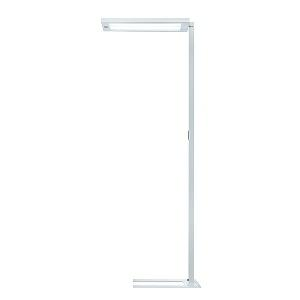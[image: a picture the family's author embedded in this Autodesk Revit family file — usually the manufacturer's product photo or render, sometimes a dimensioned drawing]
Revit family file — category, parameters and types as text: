
# Revit family: lavigo_-_dps_9000_840_d_g2_00807247_5373
name_source: partatom
category: Lighting Fixtures
units: mm (PartAtom-declared; Revit-internal decimal feet)

## family parameters
Cut with Voids When Loaded = No
Host = Face
Light Source = No
Part Type = Normal
Room Calculation Point = No
Round Connector Dimension = Use Diameter
Shared = No

## types (1)
- LAVIGO - DPS 9000/840/D/G2 (1 x LED, 8950 lm, 4000K)
    Apparent Load = 63 VA
    CIE Flux Codes = 60 87 97 20 100
    Color Rendering = 80-89
    Color Temperature = 4000K
    Control Gear = Electronic ballast
    Default Elevation = 1800 mm
    Description = DPS 9000/840/D/G2|Free-standing luminaire|light source: LED|work equipment: Electronic ballast|connected load: 220-240 V, 50/60 Hz|Power consumption: approx. 63 W|standby: approx. 0,50|power factor: approx. 0,910|luminous flux: 8950 lm|luminous efficacy: 142 lm/W|light distribution: Direct/indirect|direct ratio: approx. 20 %|colour temperature: Cold white, ca. 4000 K|color rendering index (CRI): >= 80|chromaticity tolerance:  3 SDCM|technology: Continuously dimmable|operation: Multi-function switch|luminaire body|material: Steel/plastic|surface: Painted|colour: White|lamp cover: Acrylic (PMMA), Satine|tubular section|material: Steel tube|surface: Painted|Form: Tubular section upright|colour of tubular section: White|luminaire base|Form: C-form flat|weight (net): approx. 19.7 kg|mains lead: 3.00 m Mains plug CEE 7/VII|Fastening: Floor standing base|decorative contrast side parts: Flint grey|glare control: Prism aperture|luminance(L65): <= 3000 cd/m|unified glare rating(4H 8H): <=  16|special features: Luminaire head detachable, Cradle to Cradle Certified TM, Direct light component with edge light and light-guide technology for homogenous light exit, Flicker-free, Separated, direct and indirect light individually adjustable|
    Frequency = 50 Hz
    Height = 36 mm
    Lamp = 1 x LED
    Lamp Light Flux = 8950 lm
    Lamp count = 1
    Length = 675 mm
    Luminous efficacy = 142 lm/W
    Manufacturer = Waldmann
    ModVariant = No
    Model = 00807247
    Mounting Place = Floor
    Mounting Type = Freestanding
    Number of Poles = 1
    OnlyDefault = Yes
    Power Factor = 1
    Product Name = LAVIGO - DPS 9000/840/D/G2
    Product group = Free standing luminaire
    ProductGroupID = 13
    Protection Class = Protection class I
    Protection Degree = IP 20
    RLX_Detail_Level = 1
    RLX_Emergency_Light_Flux = 0 lm
    RLX_Emergency_Type = 0
    RLX_Emergency_Type_DB = No
    RlxData = <blob elided: 37253 chars, md5=102cf466>
    Socket = socket
    Standby Power = 0 W
    System Light Flux = 8950 lm
    System Power = 63 W
    Type Comments = Product without accessories
    Type Image = 121695000-00610208.jpg
    URL = http://relux.com
    VarID = ---
    Voltage = 230 V
    Voltage Range = 220-240 V
    Weight = 0.00 kg
    Width = 320 mm

## geometry (parser evidence)
native form markers: Blend x4, Sweep x14
no freeform markers — native parametric forms only
